# Revit family: NXDS_Series
name_source: partatom
category: Lighting Devices
units: mm (PartAtom-declared; Revit-internal decimal feet)

## family parameters
Cut with Voids When Loaded = No
Host = Face
Maintain Annotation Orientation = Yes
OmniClass Number = 23.85.80.11.27
OmniClass Title = Lighting Controls
Part Type = Normal
Room Calculation Point = No
Round Connector Dimension = Use Diameter
Shared = No

## types (1)
- NXDS Series
    Apparent Load = 0.000 VA
    Assembly Code = D5020
    Certifications = UL and cUL listed
    Connector Description 1 = Power Supply
    Connector Description 2 = Controls
    Construction = Protective hard plastic cover and housing
    Default Elevation = 48 "
    Description = Daylight Sensor
    Device Material = Plastic -  White
    Glass = Plastic -  Polyethylene
    Load Classification = Other
    Manufacturer = NX Lighting Controls
    Model = NXDS Series
    Operating Environment = NXDS: Indoor use only 0° to +40°;NXDS-O: Outdoor Use 40° to +50°
    Power Factor = 1
    Type Comments = Lighting Device
    URL = https://www.currentlighting.com
    Voltage = 0 V
    Warranty = Five-year limited

## geometry (parser evidence)
native form markers: Sweep x3
no freeform markers — native parametric forms only
